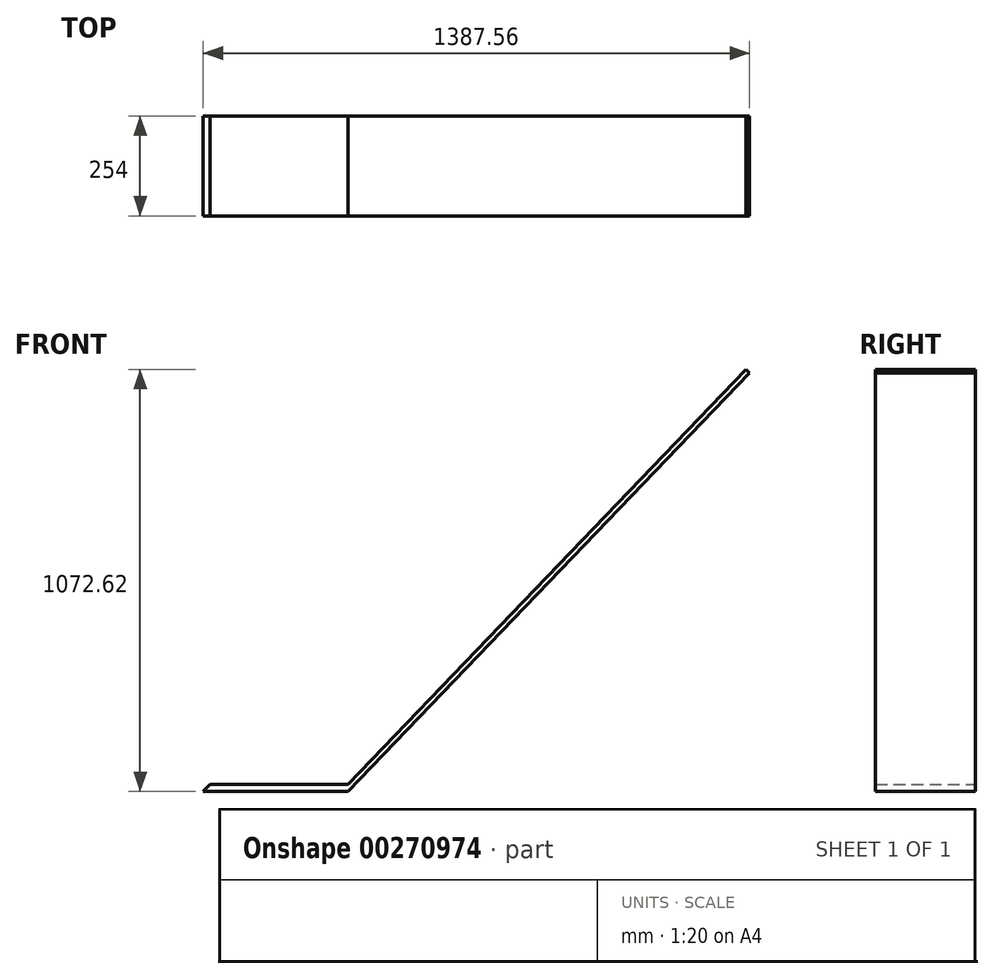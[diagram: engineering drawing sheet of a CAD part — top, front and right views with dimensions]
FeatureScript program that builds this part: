
annotation { "Feature Type Name" : "Feature", "Feature Type Description" : "" }
export const myFeature = defineFeature(function(context is Context, id is Id, definition is map)
    precondition{}
    {
        {
            var Q0;
            Q0=qCreatedBy(makeId("Front.planeOp"),FACE);
            var sketch = newSketch(context, id + "F0", { "sketchPlane" : qUnion([Q0])});
            skLineSegment(sketch, "E0", {"start": v(0, 0) * mm, "end": v(1019.44, 1063.51) * mm});
            skLineSegment(sketch, "E1", {"start": v(0, 0) * mm, "end": v(-368.12, 0) * mm});
            skLineSegment(sketch, "E2", {"start": v(-368.12, 0) * mm, "end": v(-350.55, 18.34) * mm});
            skLineSegment(sketch, "E3", {"start": v(-350.55, 18.34) * mm, "end": v(0, 18.34) * mm});
            skLineSegment(sketch, "E4", {"start": v(0, 18.34) * mm, "end": v(1010.6, 1072.62) * mm});
            skLineSegment(sketch, "E5", {"start": v(1010.6, 1072.62) * mm, "end": v(1019.44, 1063.51) * mm});
            skSolve(sketch);
        }
        {
            var Q0;
            Q0 = qSketchRegion(id + "F0", true);
            extrude(context, id + "F1", {"entities" : qUnion([Q0]), "depth" : 254 * mm});
        }
    });
